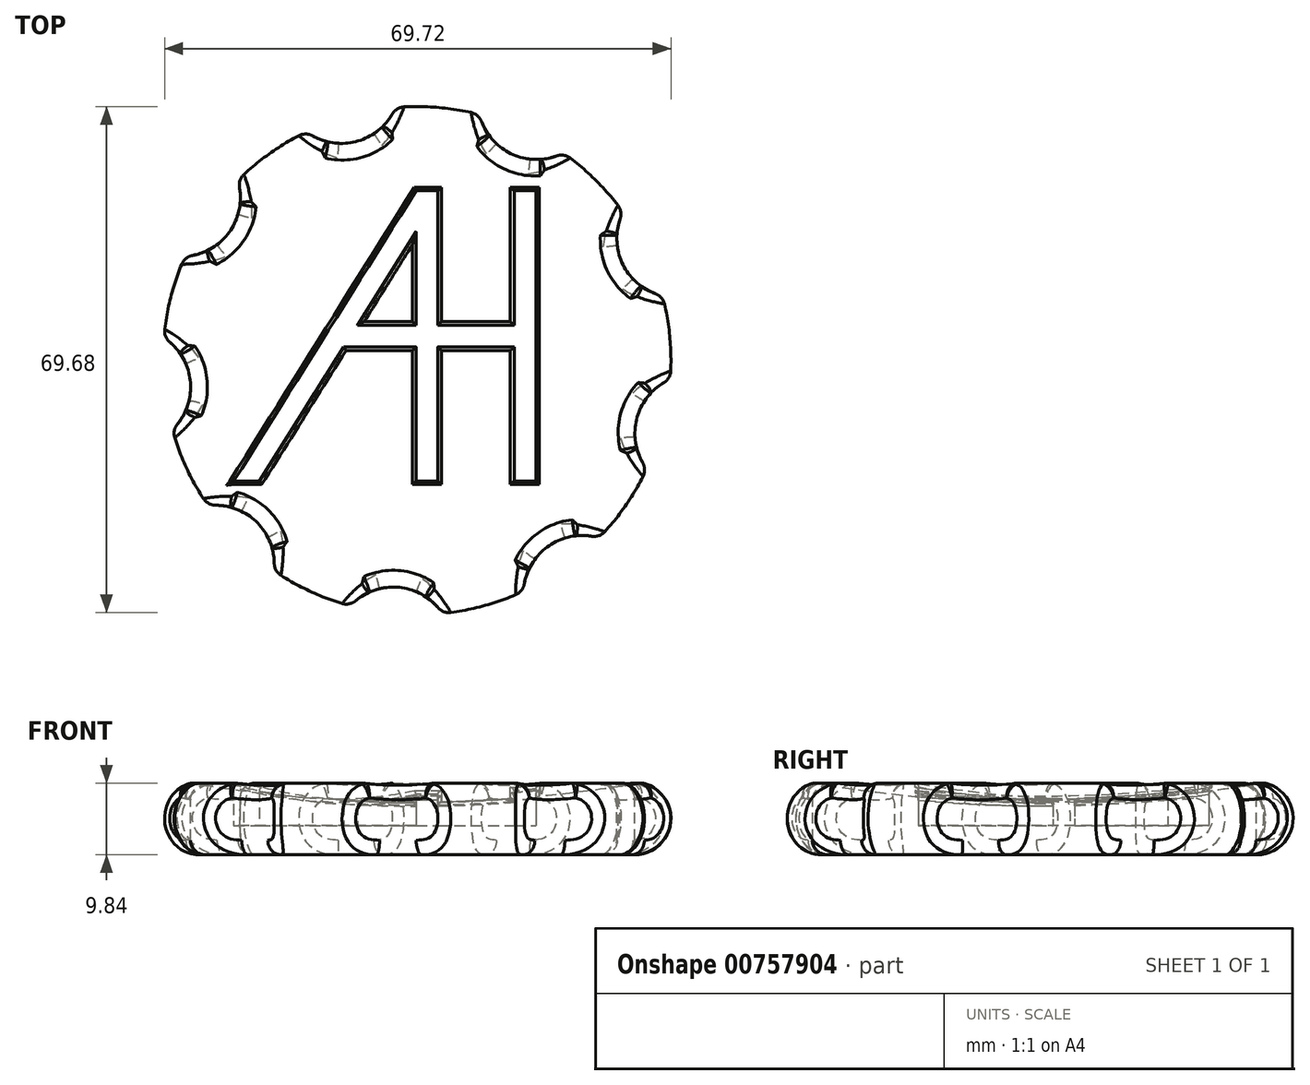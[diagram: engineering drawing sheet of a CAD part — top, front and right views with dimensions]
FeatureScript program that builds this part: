
annotation { "Feature Type Name" : "Feature", "Feature Type Description" : "" }
export const myFeature = defineFeature(function(context is Context, id is Id, definition is map)
    precondition{}
    {
        {
            var Q0;
            Q0=qCreatedBy(makeId("Top.planeOp"),FACE);
            var sketch = newSketch(context, id + "F0", { "sketchPlane" : qUnion([Q0])});
            skLineSegment(sketch, "E0.bottom", {"start": v(15, 1.5) * mm, "end": v(-15, 1.5) * mm, "construction": true});
            skLineSegment(sketch, "E0.top", {"start": v(15, -1.5) * mm, "end": v(-15, -1.5) * mm, "construction": true});
            skLineSegment(sketch, "E0.left", {"start": v(15, 1.5) * mm, "end": v(15, -1.5) * mm, "construction": true});
            skLineSegment(sketch, "E0.right", {"start": v(-15, 1.5) * mm, "end": v(-15, -1.5) * mm, "construction": true});
            skPoint(sketch, "E0.middle", {"position": v(0, 0) * mm});
            skLineSegment(sketch, "E1.bottom", {"start": v(1.5, 20) * mm, "end": v(-1.5, 20) * mm, "construction": true});
            skLineSegment(sketch, "E1.top", {"start": v(1.5, -20) * mm, "end": v(-1.5, -20) * mm, "construction": true});
            skLineSegment(sketch, "E1.left", {"start": v(1.5, 20) * mm, "end": v(1.5, -20) * mm, "construction": true});
            skLineSegment(sketch, "E1.right", {"start": v(-1.5, 20) * mm, "end": v(-1.5, -20) * mm, "construction": true});
            skLineSegment(sketch, "E2.bottom", {"start": v(15, 20) * mm, "end": v(12, 20) * mm, "construction": true});
            skLineSegment(sketch, "E2.top", {"start": v(15, -20) * mm, "end": v(12, -20) * mm, "construction": true});
            skLineSegment(sketch, "E2.left", {"start": v(15, 20) * mm, "end": v(15, -20) * mm, "construction": true});
            skLineSegment(sketch, "E2.right", {"start": v(12, 20) * mm, "end": v(12, -20) * mm, "construction": true});
            skPoint(sketch, "E2.middle", {"position": v(13.5, 0) * mm});
            skLineSegment(sketch, "E3", {"start": v(-1.5, 20) * mm, "end": v(1.5, 20) * mm, "construction": true});
            skLineSegment(sketch, "E4", {"start": v(1.5, 1.5) * mm, "end": v(12, 1.5) * mm, "construction": true});
            skLineSegment(sketch, "E5", {"start": v(12, 1.5) * mm, "end": v(12, 20) * mm, "construction": true});
            skLineSegment(sketch, "E6", {"start": v(12, -20) * mm, "end": v(12, -1.5) * mm, "construction": true});
            skLineSegment(sketch, "E7", {"start": v(12, -1.5) * mm, "end": v(1.5, -1.5) * mm, "construction": true});
            skLineSegment(sketch, "E8", {"start": v(1.5, -1.5) * mm, "end": v(1.5, -20) * mm, "construction": true});
            skLineSegment(sketch, "E9", {"start": v(-1.5, -20) * mm, "end": v(-1.5, -1.5) * mm, "construction": true});
            skLineSegment(sketch, "E10", {"start": v(-1.5, -1.5) * mm, "end": v(-15, -1.5) * mm, "construction": true});
            skLineSegment(sketch, "E11", {"start": v(1.5, 20) * mm, "end": v(1.5, 1.5) * mm, "construction": true});
            skLineSegment(sketch, "E12", {"start": v(-15, -1.5) * mm, "end": v(-15, -1.5) * mm});
            skLineSegment(sketch, "E13", {"start": v(-1.5, -20) * mm, "end": v(1.5, -20) * mm, "construction": true});
            skLineSegment(sketch, "E14", {"start": v(12, -20) * mm, "end": v(15, -20) * mm, "construction": true});
            skLineSegment(sketch, "E15", {"start": v(12, 20) * mm, "end": v(15, 20) * mm, "construction": true});
            skLineSegment(sketch, "E16", {"start": v(-15, 1.5) * mm, "end": v(-11.59, 1.5) * mm, "construction": true});
            skLineSegment(sketch, "E17", {"start": v(-1.5, 20) * mm, "end": v(-15, -1.5) * mm, "construction": true});
            skLineSegment(sketch, "E18", {"start": v(-15, -1.5) * mm, "end": v(-31, -27) * mm, "construction": true});
            skLineSegment(sketch, "E19", {"start": v(-1.5, 20) * mm, "end": v(-26.62, -20) * mm});
            skLineSegment(sketch, "E20", {"start": v(-26.62, -20) * mm, "end": v(-23.07, -20) * mm});
            skLineSegment(sketch, "E21", {"start": v(-23.07, -20) * mm, "end": v(-11.46, -1.5) * mm});
            skLineSegment(sketch, "E22", {"start": v(-11.46, -1.5) * mm, "end": v(-1.5, -1.5) * mm});
            skLineSegment(sketch, "E23", {"start": v(-1.5, -20) * mm, "end": v(1.5, -20) * mm});
            skLineSegment(sketch, "E24", {"start": v(1.5, -1.5) * mm, "end": v(12, -1.5) * mm});
            skLineSegment(sketch, "E25", {"start": v(12, -20) * mm, "end": v(15, -20) * mm});
            skLineSegment(sketch, "E26", {"start": v(15, 20) * mm, "end": v(12, 20) * mm});
            skLineSegment(sketch, "E27", {"start": v(12, 1.5) * mm, "end": v(1.5, 1.5) * mm});
            skLineSegment(sketch, "E28", {"start": v(1.5, 20) * mm, "end": v(-1.5, 20) * mm});
            skLineSegment(sketch, "E29", {"start": v(1.5, 20) * mm, "end": v(1.5, 1.5) * mm});
            skLineSegment(sketch, "E30", {"start": v(15, 20) * mm, "end": v(15, -20) * mm});
            skLineSegment(sketch, "E31", {"start": v(12, -20) * mm, "end": v(12, -1.5) * mm});
            skLineSegment(sketch, "E32", {"start": v(1.5, -1.5) * mm, "end": v(1.5, -20) * mm});
            skLineSegment(sketch, "E33", {"start": v(-1.5, -20) * mm, "end": v(-1.5, -1.5) * mm});
            skLineSegment(sketch, "E34", {"start": v(12, 1.5) * mm, "end": v(12, 20) * mm});
            skLineSegment(sketch, "E35", {"start": v(-23.07, -20) * mm, "end": v(-0.29, 16.29) * mm, "construction": true});
            skLineSegment(sketch, "E36", {"start": v(-1.5, 1.5) * mm, "end": v(-1.5, 14.36) * mm});
            skLineSegment(sketch, "E37", {"start": v(-1.5, 14.36) * mm, "end": v(-9.57, 1.5) * mm});
            skLineSegment(sketch, "E38", {"start": v(-9.57, 1.5) * mm, "end": v(-1.5, 1.5) * mm});
            skSolve(sketch);
        }
        {
            var Q0;
            Q0=makeQuery(id+"F0.imprint","IMPRINT",FACE,{"disambiguationData":[TD([[makeQuery(id+"F0.imprint","IMPRINT",EDGE,{"derivedFrom":sQuery(id+"F0.wireOp",EDGE,"E19")}),1.0]])]});
            extrude(context, id + "F1", {"entities" : qUnion([Q0]), "depth" : 12 * mm, "offsetDistance" : 25 * mm});
        }
        {
            var Q0;
            Q0=qCreatedBy(makeId("Top.planeOp"),FACE);
            var sketch = newSketch(context, id + "F2", { "sketchPlane" : qUnion([Q0])});
            skCircle(sketch, "E39", {"center": v(0, 0) * mm, "radius": 34.99 * mm});
            skSolve(sketch);
        }
        {
            var Q0;
            Q0=makeQuery(id+"F2.imprint","IMPRINT",FACE,{"disambiguationData":[TD([[makeQuery(id+"F2.imprint","IMPRINT",EDGE,{"derivedFrom":sQuery(id+"F2.wireOp",EDGE,"E39")}),1.0]])]});
            extrude(context, id + "F3", {"entities" : qUnion([Q0]), "depth" : 10 * mm, "offsetDistance" : 25 * mm});
        }
        {
            var Q0;
            Q0=makeQuery(id+"F3.opExtrude","SWEPT_FACE",FACE,{"disambiguationData":[OSD([sQuery(id+"F2.wireOp",EDGE,"E39")])]});
            fillet(context, id + "F4", {"entities" : qUnion([Q0]), "radius" : 5 * mm, "tangentPropagation" : true, "allowEdgeOverflow" : false});
        }
        {
            var Q0;
            Q0=qCreatedBy(makeId("Right.planeOp"),FACE);
            var sketch = newSketch(context, id + "F5", { "sketchPlane" : qUnion([Q0])});
            skArc(sketch, "E40", {"start": v(0, 7.17) * mm, "mid": v(15.62, 7.9) * mm, "end": v(31.13, 9.9) * mm});
            skLineSegment(sketch, "E41", {"start": v(31.13, 9.9) * mm, "end": v(24.7, 21.48) * mm});
            skLineSegment(sketch, "E42", {"start": v(24.7, 21.48) * mm, "end": v(0, 22.3) * mm});
            skLineSegment(sketch, "E43", {"start": v(0, 28.3) * mm, "end": v(0, -9.27) * mm, "construction": true});
            skPoint(sketch, "E44.end.orphan", {"position": v(-34.02, 9.9) * mm});
            skLineSegment(sketch, "E45", {"start": v(0, 22.3) * mm, "end": v(0, 7.17) * mm});
            skSolve(sketch);
        }
        {
            var Q0;
            Q0 = qSketchRegion(id + "F5", true);
            var Q1;
            Q1=sQuery(id+"F5.wireOp",EDGE,"E43");
            revolve(context, id + "F6", {"operationType" : NewBodyOperationType.REMOVE, "surfaceOperationType" : NewSurfaceOperationType.NEW, "entities" : qUnion([Q0]), "axis" : qUnion([Q1]), "revolveType" : RevolveType.FULL, "oppositeDirection" : true});
        }
        {
            var Q0;
            Q0=makeQuery(id+"F6.boolean.opBoolean","INTERSECT",EDGE,{"derivedFrom":[makeQuery(id+"F4.opFillet","BLEND_FACE",FACE,{"disambiguationData":[OSD([sQuery(id+"F2.wireOp",EDGE,"E39")])]}),makeQuery(id+"F6.opRevolve","SWEPT_FACE",FACE,{"disambiguationData":[OSD([sQuery(id+"F5.wireOp",EDGE,"E40")])]})]});
            fillet(context, id + "F7", {"entities" : qUnion([Q0]), "radius" : 2 * mm, "tangentPropagation" : true, "allowEdgeOverflow" : false});
        }
        {
            var Q0;
            Q0=qCreatedBy(makeId("Top.planeOp"),FACE);
            var sketch = newSketch(context, id + "F8", { "sketchPlane" : qUnion([Q0])});
            skCircle(sketch, "E46.0", {"center": v(0, 0) * mm, "radius": 34.99 * mm, "construction": true});
            skCircle(sketch, "E47", {"center": v(-32.4, 22.45) * mm, "radius": 8.1 * mm});
            skCircle(sketch, "E48.1.0", {"center": v(-39.25, -3.63) * mm, "radius": 8.1 * mm});
            skCircle(sketch, "E48.2.0", {"center": v(-27.73, -28) * mm, "radius": 8.1 * mm});
            skCircle(sketch, "E48.3.0", {"center": v(-3.24, -39.28) * mm, "radius": 8.1 * mm});
            skCircle(sketch, "E48.4.0", {"center": v(22.77, -32.17) * mm, "radius": 8.1 * mm});
            skCircle(sketch, "E48.5.0", {"center": v(38.12, -10.01) * mm, "radius": 8.1 * mm});
            skCircle(sketch, "E48.6.0", {"center": v(35.64, 16.83) * mm, "radius": 8.1 * mm});
            skCircle(sketch, "E48.7.0", {"center": v(16.48, 35.8) * mm, "radius": 8.1 * mm});
            skCircle(sketch, "E48.8.0", {"center": v(-10.39, 38.02) * mm, "radius": 8.1 * mm});
            skSolve(sketch);
        }
        {
            var Q0;
            Q0 = qSketchRegion(id + "F8", true);
            extrude(context, id + "F9", {"entities" : qUnion([Q0]), "endBound" : BoundingType.SYMMETRIC, "oppositeDirection" : true, "depth" : 25 * mm, "offsetDistance" : 25 * mm});
        }
        {
            var Q0;
            Q0=makeQuery(id+"F9.opExtrude","SWEPT_BODY",BODY,{"disambiguationData":[OSD([sQuery(id+"F8.wireOp",EDGE,"E48.8.0")])]});
            var Q1;
            Q1=makeQuery(id+"F9.opExtrude","SWEPT_BODY",BODY,{"disambiguationData":[OSD([sQuery(id+"F8.wireOp",EDGE,"E48.7.0")])]});
            var Q2;
            Q2=makeQuery(id+"F9.opExtrude","SWEPT_BODY",BODY,{"disambiguationData":[OSD([sQuery(id+"F8.wireOp",EDGE,"E48.6.0")])]});
            var Q3;
            Q3=makeQuery(id+"F9.opExtrude","SWEPT_BODY",BODY,{"disambiguationData":[OSD([sQuery(id+"F8.wireOp",EDGE,"E48.5.0")])]});
            var Q4;
            Q4=makeQuery(id+"F9.opExtrude","SWEPT_BODY",BODY,{"disambiguationData":[OSD([sQuery(id+"F8.wireOp",EDGE,"E48.4.0")])]});
            var Q5;
            Q5=makeQuery(id+"F9.opExtrude","SWEPT_BODY",BODY,{"disambiguationData":[OSD([sQuery(id+"F8.wireOp",EDGE,"E48.3.0")])]});
            var Q6;
            Q6=makeQuery(id+"F9.opExtrude","SWEPT_BODY",BODY,{"disambiguationData":[OSD([sQuery(id+"F8.wireOp",EDGE,"E48.2.0")])]});
            var Q7;
            Q7=makeQuery(id+"F9.opExtrude","SWEPT_BODY",BODY,{"disambiguationData":[OSD([sQuery(id+"F8.wireOp",EDGE,"E48.1.0")])]});
            var Q8;
            Q8=makeQuery(id+"F9.opExtrude","SWEPT_BODY",BODY,{"disambiguationData":[OSD([sQuery(id+"F8.wireOp",EDGE,"E47")])]});
            var Q9;
            Q9=makeQuery(id+"F3.opExtrude","SWEPT_BODY",BODY,{"disambiguationData":[OSD([sQuery(id+"F2.wireOp",EDGE,"E39")])]});
            booleanBodies(context, id + "F10", {"operationType" : BooleanOperationType.SUBTRACTION, "tools" : qUnion([Q0, Q1, Q2, Q3, Q4, Q5, Q6, Q7, Q8]), "targets" : qUnion([Q9])});
        }
        {
            var Q0;
            Q0=makeQuery(id+"F10.opBoolean","INTERSECT",EDGE,{"derivedFrom":[makeQuery(id+"F4.opFillet","BLEND_FACE",FACE,{"disambiguationData":[OSD([sQuery(id+"F2.wireOp",EDGE,"E39")])]}),makeQuery(id+"F9.opExtrude","SWEPT_FACE",FACE,{"disambiguationData":[OSD([sQuery(id+"F8.wireOp",EDGE,"E47")])]})]});
            var Q1;
            Q1=makeQuery(id+"F10.opBoolean","INTERSECT",EDGE,{"derivedFrom":[makeQuery(id+"F4.opFillet","BLEND_FACE",FACE,{"disambiguationData":[OSD([sQuery(id+"F2.wireOp",EDGE,"E39")])]}),makeQuery(id+"F9.opExtrude","SWEPT_FACE",FACE,{"disambiguationData":[OSD([sQuery(id+"F8.wireOp",EDGE,"E48.8.0")])]})]});
            var Q2;
            Q2=makeQuery(id+"F10.opBoolean","INTERSECT",EDGE,{"derivedFrom":[makeQuery(id+"F4.opFillet","BLEND_FACE",FACE,{"disambiguationData":[OSD([sQuery(id+"F2.wireOp",EDGE,"E39")])]}),makeQuery(id+"F9.opExtrude","SWEPT_FACE",FACE,{"disambiguationData":[OSD([sQuery(id+"F8.wireOp",EDGE,"E48.7.0")])]})]});
            var Q3;
            Q3=makeQuery(id+"F10.opBoolean","INTERSECT",EDGE,{"derivedFrom":[makeQuery(id+"F4.opFillet","BLEND_FACE",FACE,{"disambiguationData":[OSD([sQuery(id+"F2.wireOp",EDGE,"E39")])]}),makeQuery(id+"F9.opExtrude","SWEPT_FACE",FACE,{"disambiguationData":[OSD([sQuery(id+"F8.wireOp",EDGE,"E48.6.0")])]})]});
            var Q4;
            Q4=makeQuery(id+"F10.opBoolean","INTERSECT",EDGE,{"derivedFrom":[makeQuery(id+"F4.opFillet","BLEND_FACE",FACE,{"disambiguationData":[OSD([sQuery(id+"F2.wireOp",EDGE,"E39")])]}),makeQuery(id+"F9.opExtrude","SWEPT_FACE",FACE,{"disambiguationData":[OSD([sQuery(id+"F8.wireOp",EDGE,"E48.5.0")])]})]});
            var Q5;
            Q5=makeQuery(id+"F10.opBoolean","INTERSECT",EDGE,{"derivedFrom":[makeQuery(id+"F4.opFillet","BLEND_FACE",FACE,{"disambiguationData":[OSD([sQuery(id+"F2.wireOp",EDGE,"E39")])]}),makeQuery(id+"F9.opExtrude","SWEPT_FACE",FACE,{"disambiguationData":[OSD([sQuery(id+"F8.wireOp",EDGE,"E48.4.0")])]})]});
            var Q6;
            Q6=makeQuery(id+"F10.opBoolean","INTERSECT",EDGE,{"derivedFrom":[makeQuery(id+"F4.opFillet","BLEND_FACE",FACE,{"disambiguationData":[OSD([sQuery(id+"F2.wireOp",EDGE,"E39")])]}),makeQuery(id+"F9.opExtrude","SWEPT_FACE",FACE,{"disambiguationData":[OSD([sQuery(id+"F8.wireOp",EDGE,"E48.3.0")])]})]});
            var Q7;
            Q7=makeQuery(id+"F10.opBoolean","INTERSECT",EDGE,{"derivedFrom":[makeQuery(id+"F4.opFillet","BLEND_FACE",FACE,{"disambiguationData":[OSD([sQuery(id+"F2.wireOp",EDGE,"E39")])]}),makeQuery(id+"F9.opExtrude","SWEPT_FACE",FACE,{"disambiguationData":[OSD([sQuery(id+"F8.wireOp",EDGE,"E48.2.0")])]})]});
            var Q8;
            Q8=makeQuery(id+"F10.opBoolean","INTERSECT",EDGE,{"derivedFrom":[makeQuery(id+"F4.opFillet","BLEND_FACE",FACE,{"disambiguationData":[OSD([sQuery(id+"F2.wireOp",EDGE,"E39")])]}),makeQuery(id+"F9.opExtrude","SWEPT_FACE",FACE,{"disambiguationData":[OSD([sQuery(id+"F8.wireOp",EDGE,"E48.1.0")])]})]});
            fillet(context, id + "F11", {"entities" : qUnion([Q0, Q1, Q2, Q3, Q4, Q5, Q6, Q7, Q8]), "radius" : 2 * mm, "tangentPropagation" : true, "allowEdgeOverflow" : false});
        }
        {
            var Q0;
            Q0=makeQuery(id+"F1.opExtrude","SWEPT_BODY",BODY,{"disambiguationData":[OSD([sQuery(id+"F0.wireOp",EDGE,"E19"),sQuery(id+"F0.wireOp",EDGE,"E20"),sQuery(id+"F0.wireOp",EDGE,"E21"),sQuery(id+"F0.wireOp",EDGE,"E22"),sQuery(id+"F0.wireOp",EDGE,"E23"),sQuery(id+"F0.wireOp",EDGE,"E24"),sQuery(id+"F0.wireOp",EDGE,"E25"),sQuery(id+"F0.wireOp",EDGE,"E26"),sQuery(id+"F0.wireOp",EDGE,"E27"),sQuery(id+"F0.wireOp",EDGE,"E28"),sQuery(id+"F0.wireOp",EDGE,"E29"),sQuery(id+"F0.wireOp",EDGE,"E30"),sQuery(id+"F0.wireOp",EDGE,"E31"),sQuery(id+"F0.wireOp",EDGE,"E32"),sQuery(id+"F0.wireOp",EDGE,"E33"),sQuery(id+"F0.wireOp",EDGE,"E34"),sQuery(id+"F0.wireOp",EDGE,"E36"),sQuery(id+"F0.wireOp",EDGE,"E37"),sQuery(id+"F0.wireOp",EDGE,"E38")])]});
            transform(context, id + "F12", {"entities" : qUnion([Q0]), "transformType" : TransformType.TRANSLATION_3D, "dx" : 1.4 * mm, "dy" : 3.4 * mm, "dz" : 4 * mm, "makeCopy" : false});
        }
        {
            var Q0;
            Q0=makeQuery(id+"F1.opExtrude","SWEPT_BODY",BODY,{"disambiguationData":[OSD([sQuery(id+"F0.wireOp",EDGE,"E19"),sQuery(id+"F0.wireOp",EDGE,"E20"),sQuery(id+"F0.wireOp",EDGE,"E21"),sQuery(id+"F0.wireOp",EDGE,"E22"),sQuery(id+"F0.wireOp",EDGE,"E23"),sQuery(id+"F0.wireOp",EDGE,"E24"),sQuery(id+"F0.wireOp",EDGE,"E25"),sQuery(id+"F0.wireOp",EDGE,"E26"),sQuery(id+"F0.wireOp",EDGE,"E27"),sQuery(id+"F0.wireOp",EDGE,"E28"),sQuery(id+"F0.wireOp",EDGE,"E29"),sQuery(id+"F0.wireOp",EDGE,"E30"),sQuery(id+"F0.wireOp",EDGE,"E31"),sQuery(id+"F0.wireOp",EDGE,"E32"),sQuery(id+"F0.wireOp",EDGE,"E33"),sQuery(id+"F0.wireOp",EDGE,"E34"),sQuery(id+"F0.wireOp",EDGE,"E36"),sQuery(id+"F0.wireOp",EDGE,"E37"),sQuery(id+"F0.wireOp",EDGE,"E38")])]});
            var Q1;
            Q1=makeQuery(id+"F3.opExtrude","SWEPT_BODY",BODY,{"disambiguationData":[OSD([sQuery(id+"F2.wireOp",EDGE,"E39")])]});
            booleanBodies(context, id + "F13", {"operationType" : BooleanOperationType.SUBTRACTION, "tools" : qUnion([Q0]), "targets" : qUnion([Q1])});
        }
        {
            var Q0;
            {var subQ1=sQuery(id+"F5.wireOp",EDGE,"E40");Q0=makeQuery(id+"F13.opBoolean","SPLIT",FACE,{"disambiguationData":[TD([makeQuery(id+"F1.opExtrude","SWEPT_FACE",FACE,{"disambiguationData":[OSD([sQuery(id+"F0.wireOp",EDGE,"E19")])]})])],"derivedFrom":makeQuery(id+"F6.boolean.opBoolean","COPY",FACE,{"derivedFrom":makeQuery(id+"F6.opRevolve","SWEPT_FACE",FACE,{"disambiguationData":[OSD([subQ1])]})})});}
            var Q1;
            Q1=makeQuery(id+"F13.opBoolean","SPLIT",FACE,{"disambiguationData":[TD([makeQuery(id+"F1.opExtrude","SWEPT_FACE",FACE,{"disambiguationData":[OSD([sQuery(id+"F0.wireOp",EDGE,"E36")])]})])],"derivedFrom":makeQuery(id+"F6.boolean.opBoolean","COPY",FACE,{"derivedFrom":makeQuery(id+"F6.opRevolve","SWEPT_FACE",FACE,{"disambiguationData":[OSD([sQuery(id+"F5.wireOp",EDGE,"E40")])]})})});
            fillet(context, id + "F14", {"entities" : qUnion([Q0, Q1]), "radius" : .5 * mm, "tangentPropagation" : true, "allowEdgeOverflow" : false});
        }
    });
